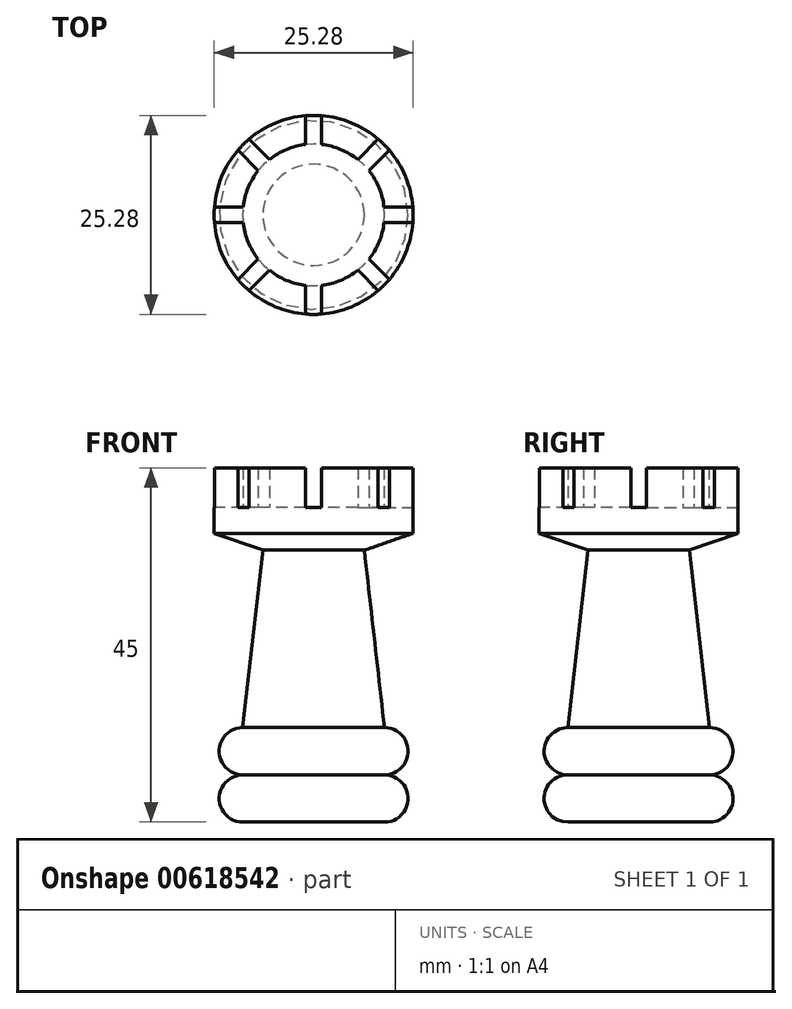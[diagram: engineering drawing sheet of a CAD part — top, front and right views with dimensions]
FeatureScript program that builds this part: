
annotation { "Feature Type Name" : "Feature", "Feature Type Description" : "" }
export const myFeature = defineFeature(function(context is Context, id is Id, definition is map)
    precondition{}
    {
        {
            var Q0;
            Q0=qCreatedBy(makeId("Front.planeOp"),FACE);
            var sketch = newSketch(context, id + "F0", { "sketchPlane" : qUnion([Q0])});
            skLineSegment(sketch, "E0", {"start": v(0, 0) * mm, "end": v(9, 0) * mm});
            skArc(sketch, "E1", {"start": v(9, 0) * mm, "mid": v(12, 3) * mm, "end": v(9, 6) * mm});
            skArc(sketch, "E2", {"start": v(9, 6) * mm, "mid": v(12, 9) * mm, "end": v(9, 12) * mm});
            skLineSegment(sketch, "E3", {"start": v(12.64, 40) * mm, "end": v(0, 40) * mm});
            skLineSegment(sketch, "E4", {"start": v(0, 40) * mm, "end": v(0, 0) * mm});
            skLineSegment(sketch, "E5", {"start": v(9, 12) * mm, "end": v(6.44, 34.54) * mm});
            skLineSegment(sketch, "E6", {"start": v(12.64, 40) * mm, "end": v(12.64, 36.7) * mm});
            skLineSegment(sketch, "E7", {"start": v(12.64, 36.7) * mm, "end": v(6.44, 34.54) * mm});
            skSolve(sketch);
        }
        {
            var Q0;
            Q0=makeQuery(id+"F0.imprint","IMPRINT",FACE,{"disambiguationData":[TD([[makeQuery(id+"F0.imprint","IMPRINT",EDGE,{"derivedFrom":sQuery(id+"F0.wireOp",EDGE,"E0")}),1.0]])]});
            var Q1;
            Q1=sQuery(id+"F0.wireOp",EDGE,"E4");
            revolve(context, id + "F1", {"entities" : qUnion([Q0]), "axis" : qUnion([Q1]), "revolveType" : RevolveType.FULL});
        }
        {
            var Q0;
            Q0=makeQuery(id+"F1.opRevolve","SWEPT_FACE",FACE,{"disambiguationData":[OSD([sQuery(id+"F0.wireOp",EDGE,"E3")])]});
            var sketch = newSketch(context, id + "F2", { "sketchPlane" : qUnion([Q0])});
            skArc(sketch, "E8", {"start": v(-7.03, 5.62) * mm, "mid": v(-8.31, 3.44) * mm, "end": v(-8.94, 1) * mm});
            skLineSegment(sketch, "E9", {"start": v(1, 8.94) * mm, "end": v(1, 12.6) * mm});
            skLineSegment(sketch, "E10", {"start": v(-1, 8.94) * mm, "end": v(-1, 12.6) * mm});
            skLineSegment(sketch, "E11.1.0", {"start": v(-7.03, 5.62) * mm, "end": v(-9.62, 8.2) * mm});
            skLineSegment(sketch, "E11.1.1", {"start": v(-5.62, 7.03) * mm, "end": v(-8.2, 9.62) * mm});
            skLineSegment(sketch, "E11.2.0", {"start": v(-8.94, -1) * mm, "end": v(-12.6, -1) * mm});
            skLineSegment(sketch, "E11.2.1", {"start": v(-8.94, 1) * mm, "end": v(-12.6, 1) * mm});
            skLineSegment(sketch, "E11.3.0", {"start": v(-5.62, -7.03) * mm, "end": v(-8.2, -9.62) * mm});
            skLineSegment(sketch, "E11.3.1", {"start": v(-7.03, -5.62) * mm, "end": v(-9.62, -8.2) * mm});
            skLineSegment(sketch, "E11.4.0", {"start": v(1, -8.94) * mm, "end": v(1, -12.6) * mm});
            skLineSegment(sketch, "E11.4.1", {"start": v(-1, -8.94) * mm, "end": v(-1, -12.6) * mm});
            skLineSegment(sketch, "E11.5.0", {"start": v(7.03, -5.62) * mm, "end": v(9.62, -8.2) * mm});
            skLineSegment(sketch, "E11.5.1", {"start": v(5.62, -7.03) * mm, "end": v(8.2, -9.62) * mm});
            skLineSegment(sketch, "E11.6.0", {"start": v(8.94, 1) * mm, "end": v(12.6, 1) * mm});
            skLineSegment(sketch, "E11.6.1", {"start": v(8.94, -1) * mm, "end": v(12.6, -1) * mm});
            skLineSegment(sketch, "E11.7.0", {"start": v(5.62, 7.03) * mm, "end": v(8.2, 9.62) * mm});
            skLineSegment(sketch, "E11.7.1", {"start": v(7.03, 5.62) * mm, "end": v(9.62, 8.2) * mm});
            skArc(sketch, "E12.trimOffspring", {"start": v(-8.94, -1) * mm, "mid": v(-8.31, -3.44) * mm, "end": v(-7.03, -5.62) * mm});
            skArc(sketch, "E13.trimOffspring", {"start": v(-5.62, -7.03) * mm, "mid": v(-3.44, -8.31) * mm, "end": v(-1, -8.94) * mm});
            skArc(sketch, "E14.trimOffspring", {"start": v(1, -8.94) * mm, "mid": v(3.44, -8.31) * mm, "end": v(5.62, -7.03) * mm});
            skArc(sketch, "E15.trimOffspring", {"start": v(7.03, -5.62) * mm, "mid": v(8.31, -3.44) * mm, "end": v(8.94, -1) * mm});
            skArc(sketch, "E16.trimOffspring", {"start": v(8.94, 1) * mm, "mid": v(8.31, 3.44) * mm, "end": v(7.03, 5.62) * mm});
            skArc(sketch, "E17.trimOffspring", {"start": v(5.62, 7.03) * mm, "mid": v(3.44, 8.31) * mm, "end": v(1, 8.94) * mm});
            skArc(sketch, "E18.trimOffspring", {"start": v(-1, 8.94) * mm, "mid": v(-3.44, 8.31) * mm, "end": v(-5.62, 7.03) * mm});
            skArc(sketch, "E19", {"start": v(-9.62, 8.2) * mm, "mid": v(-11.68, 4.84) * mm, "end": v(-12.6, 1) * mm});
            skArc(sketch, "E20.trimOffspring", {"start": v(-1, 12.6) * mm, "mid": v(-4.84, 11.68) * mm, "end": v(-8.2, 9.62) * mm});
            skArc(sketch, "E21.trimOffspring", {"start": v(8.2, 9.62) * mm, "mid": v(4.84, 11.68) * mm, "end": v(1, 12.6) * mm});
            skArc(sketch, "E22.trimOffspring", {"start": v(12.6, 1) * mm, "mid": v(11.68, 4.84) * mm, "end": v(9.62, 8.2) * mm});
            skArc(sketch, "E23.trimOffspring", {"start": v(9.62, -8.2) * mm, "mid": v(11.68, -4.84) * mm, "end": v(12.6, -1) * mm});
            skArc(sketch, "E24.trimOffspring", {"start": v(1, -12.6) * mm, "mid": v(4.84, -11.68) * mm, "end": v(8.2, -9.62) * mm});
            skArc(sketch, "E25.trimOffspring", {"start": v(-8.2, -9.62) * mm, "mid": v(-4.84, -11.68) * mm, "end": v(-1, -12.6) * mm});
            skArc(sketch, "E26.trimOffspring", {"start": v(-12.6, -1) * mm, "mid": v(-11.68, -4.84) * mm, "end": v(-9.62, -8.2) * mm});
            skSolve(sketch);
        }
        {
            var Q0;
            Q0=makeQuery(id+"F2.imprint","IMPRINT",FACE,{"disambiguationData":[TD([[makeQuery(id+"F2.imprint","IMPRINT",EDGE,{"derivedFrom":sQuery(id+"F2.wireOp",EDGE,"E8")}),-1.0]])]});
            var Q1;
            Q1=makeQuery(id+"F2.imprint","IMPRINT",FACE,{"disambiguationData":[TD([[makeQuery(id+"F2.imprint","IMPRINT",EDGE,{"derivedFrom":sQuery(id+"F2.wireOp",EDGE,"E10")}),1.0]])]});
            var Q2;
            Q2=makeQuery(id+"F2.imprint","IMPRINT",FACE,{"disambiguationData":[TD([[makeQuery(id+"F2.imprint","IMPRINT",EDGE,{"derivedFrom":sQuery(id+"F2.wireOp",EDGE,"E9")}),-1.0]])]});
            var Q3;
            Q3=makeQuery(id+"F2.imprint","IMPRINT",FACE,{"disambiguationData":[TD([[makeQuery(id+"F2.imprint","IMPRINT",EDGE,{"derivedFrom":sQuery(id+"F2.wireOp",EDGE,"E11.6.0")}),1.0]])]});
            var Q4;
            Q4=makeQuery(id+"F2.imprint","IMPRINT",FACE,{"disambiguationData":[TD([[makeQuery(id+"F2.imprint","IMPRINT",EDGE,{"derivedFrom":sQuery(id+"F2.wireOp",EDGE,"E11.5.0")}),1.0]])]});
            var Q5;
            Q5=makeQuery(id+"F2.imprint","IMPRINT",FACE,{"disambiguationData":[TD([[makeQuery(id+"F2.imprint","IMPRINT",EDGE,{"derivedFrom":sQuery(id+"F2.wireOp",EDGE,"E11.4.0")}),1.0]])]});
            var Q6;
            Q6=makeQuery(id+"F2.imprint","IMPRINT",FACE,{"disambiguationData":[TD([[makeQuery(id+"F2.imprint","IMPRINT",EDGE,{"derivedFrom":sQuery(id+"F2.wireOp",EDGE,"E11.3.0")}),1.0]])]});
            var Q7;
            Q7=makeQuery(id+"F2.imprint","IMPRINT",FACE,{"disambiguationData":[TD([[makeQuery(id+"F2.imprint","IMPRINT",EDGE,{"derivedFrom":sQuery(id+"F2.wireOp",EDGE,"E11.2.0")}),1.0]])]});
            extrude(context, id + "F3", {"entities" : qUnion([Q0, Q1, Q2, Q3, Q4, Q5, Q6, Q7]), "operationType" : NewBodyOperationType.ADD, "depth" : 5 * mm, "offsetDistance" : 25 * mm});
        }
    });
